# Revit family: EP-938_RFA
name_source: partatom
category: Aparatos sanitarios
units: mm (PartAtom-declared; Revit-internal decimal feet)

## family parameters
Activar corte en vistas = No
Compartido = Sí
Corte con vacíos al cargar = No
Cota de conector redondo = Usar diámetro
Mantener orientación de anotación = No
Número OmniClass = 23.45.55.14
Punto de cálculo de habitación = Sí
Se basa en plano de trabajo = Sí
Siempre vertical = Sí
Tipo de pieza = Normal
Título OmniClass = Single Faucets

## types (1)
- EP-938
    Accesorios = Inserto, herramienta de sujeción
    Características del Producto = Monomando de lavabo alto con contra de push Premier Ébano
    Comentarios de tipo = Incluye contra de push. Incluye inserto para usarse con lavabos sin rebosadero.
    Cuerpo de Latón = Brass
    Descripción = Monomando de lavabo alto con contra de push Premier Ébano
    Elevación por defecto = 1"
    Fabricante = HELVEX S.A. de C.V.
    Garantía = El producto HELVEX está garantizado, en lo que
se refiere a los acabados, por 10 axos para los
acabados cromo y duravex, y por 2 axos en
acabados diferentes al cromo y duravex.
Las piezas que sufren de desgaste natural en el
producto estin garantizadas para uso residencial
por 5 axos, y para uso comercial por 3 axos.
La vigencia de la garantia inicia a partir de la
fecha de entrega del producto al consumidor
indicada en esta Poliza de Garantta
    Imagen de tipo = EP-938.png
    Instalación = Conexión ½ - 14 NPSM
    Modelo = EP-938
    Operación = El maneral tienen una rotación horizontal para la función de agua caliente y fría; y vertical para abrir y cerrar el flujo de agua.
    Presión Máxima de Trabajo = 85.3 psi
    Presión Mínima de Trabajo = 9.9 psi
    Total Depth = 7"
    Total Height = 12"
    Total Width = 2"
    URL = https://helvex.com.mx
    Ébano = Ébano

## geometry (parser evidence)
native form markers: Sweep x2
no freeform markers — native parametric forms only
